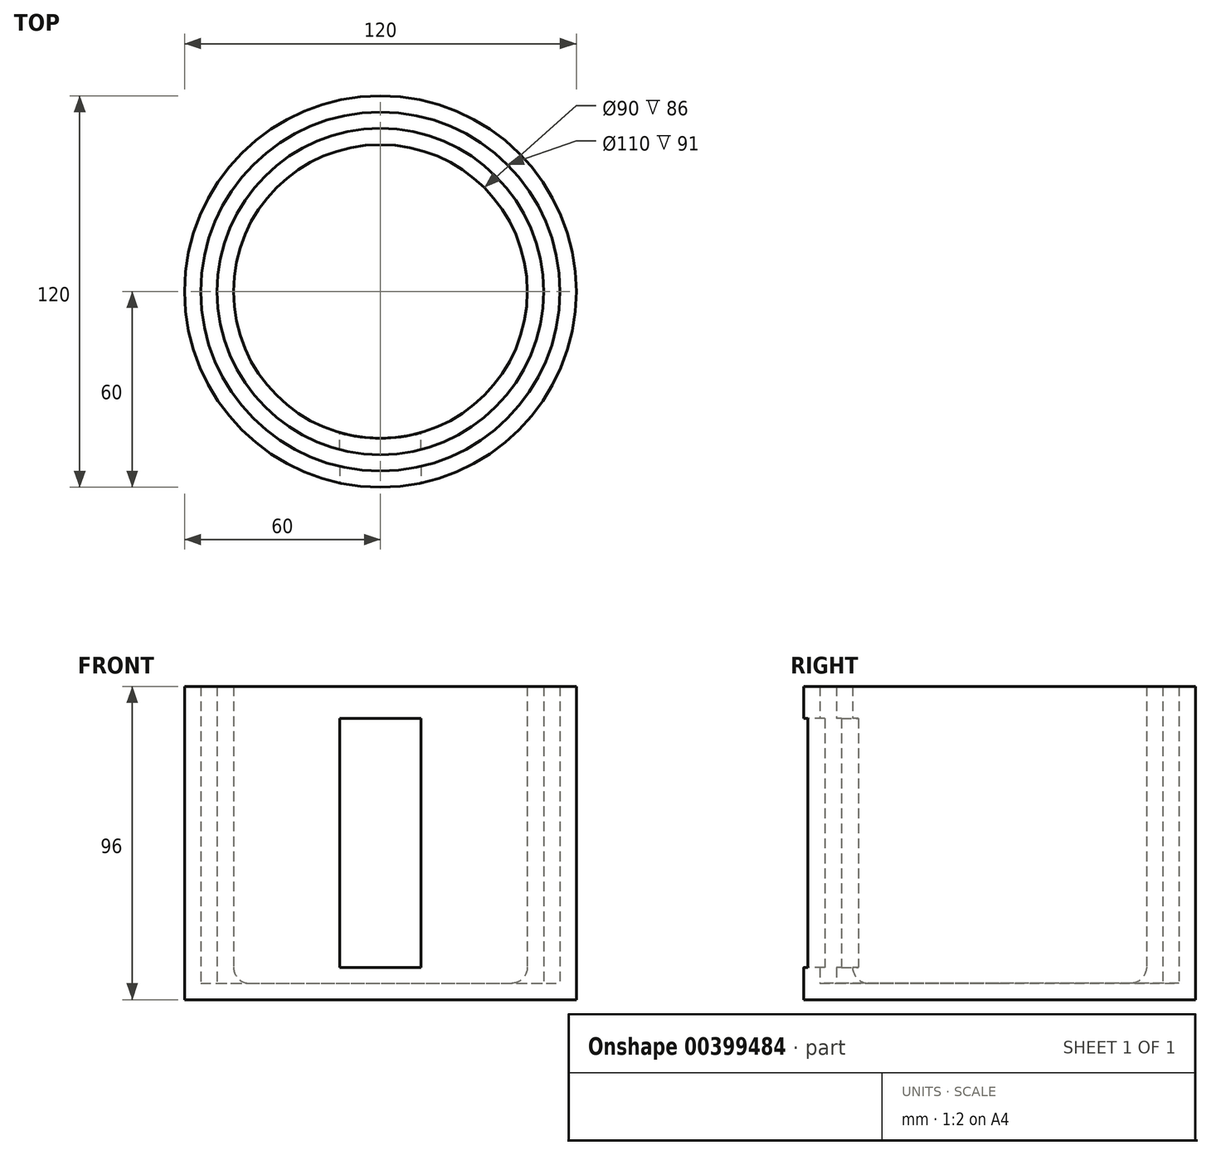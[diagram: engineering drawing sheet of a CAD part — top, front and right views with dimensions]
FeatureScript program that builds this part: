
annotation { "Feature Type Name" : "Feature", "Feature Type Description" : "" }
export const myFeature = defineFeature(function(context is Context, id is Id, definition is map)
    precondition{}
    {
        {
            var Q0;
            Q0=qCreatedBy(makeId("Front.planeOp"),FACE);
            var sketch = newSketch(context, id + "F0", { "sketchPlane" : qUnion([Q0])});
            skLineSegment(sketch, "E0", {"start": v(0, 0) * mm, "end": v(60, 0) * mm});
            skLineSegment(sketch, "E1", {"start": v(60, 0) * mm, "end": v(60, 96) * mm});
            skLineSegment(sketch, "E2.0", {"start": v(55, 5) * mm, "end": v(55, 96) * mm});
            skLineSegment(sketch, "E2.1", {"start": v(0, 5) * mm, "end": v(40, 5) * mm});
            skLineSegment(sketch, "E3", {"start": v(60, 96) * mm, "end": v(55, 96) * mm});
            skLineSegment(sketch, "E4", {"start": v(0, 0) * mm, "end": v(0, 5) * mm});
            skLineSegment(sketch, "E5.top", {"start": v(45, 96) * mm, "end": v(50, 96) * mm});
            skLineSegment(sketch, "E5.left", {"start": v(45, 10) * mm, "end": v(45, 96) * mm});
            skLineSegment(sketch, "E5.right", {"start": v(50, 5) * mm, "end": v(50, 96) * mm});
            skLineSegment(sketch, "E6.trimOffspring", {"start": v(50, 5) * mm, "end": v(55, 5) * mm});
            skPoint(sketch, "E7.visualSharp", {"position": v(45, 5) * mm});
            skArc(sketch, "E7.filletArc", {"start": v(40, 5) * mm, "mid": v(43.54, 6.46) * mm, "end": v(45, 10) * mm});
            skSolve(sketch);
        }
        {
            var Q0;
            Q0=makeQuery(id+"F0.imprint","IMPRINT",FACE,{"disambiguationData":[TD([[makeQuery(id+"F0.imprint","IMPRINT",EDGE,{"derivedFrom":sQuery(id+"F0.wireOp",EDGE,"E0")}),1.0]])]});
            var Q1;
            Q1=sQuery(id+"F0.wireOp",EDGE,"E4");
            revolve(context, id + "F1", {"entities" : qUnion([Q0]), "axis" : qUnion([Q1]), "revolveType" : RevolveType.FULL});
        }
        {
            var Q0;
            Q0=qCreatedBy(makeId("Front.planeOp"),FACE);
            var sketch = newSketch(context, id + "F2", { "sketchPlane" : qUnion([Q0])});
            skLineSegment(sketch, "E8.0", {"start": v(55, 5) * mm, "end": v(-55, 5) * mm, "construction": true});
            skLineSegment(sketch, "E9", {"start": v(-60, 0) * mm, "end": v(-60, 96) * mm, "construction": true});
            skLineSegment(sketch, "E10.bottom", {"start": v(12.5, 86.17) * mm, "end": v(-12.5, 86.17) * mm});
            skLineSegment(sketch, "E10.top", {"start": v(12.5, 9.83) * mm, "end": v(-12.5, 9.83) * mm});
            skLineSegment(sketch, "E10.left", {"start": v(12.5, 86.17) * mm, "end": v(12.5, 9.83) * mm});
            skLineSegment(sketch, "E10.right", {"start": v(-12.5, 86.17) * mm, "end": v(-12.5, 9.83) * mm});
            skPoint(sketch, "E10.middle", {"position": v(0, 48) * mm});
            skPoint(sketch, "E10.middle.positionSnap0", {"position": v(-60, 48) * mm});
            skPoint(sketch, "E10.centerSnap0", {"position": v(-60, 48) * mm});
            skSolve(sketch);
        }
        {
            var Q0;
            Q0=qSketchRegion(id+"F2",true);
            var Q1;
            Q1=makeQuery(id+"F1.opRevolve","SWEPT_FACE",FACE,{"disambiguationData":[OSD([sQuery(id+"F0.wireOp",EDGE,"E5.right")])]});
            extrude(context, id + "F3", {"entities" : qUnion([Q0]), "operationType" : NewBodyOperationType.REMOVE, "endBound" : BoundingType.UP_TO_SURFACE, "endBoundEntityFace" : qUnion([Q1]), "depth" : 25 * mm});
        }
        {
            var Q0;
            Q0=qCreatedBy(makeId("Front.planeOp"),FACE);
            cPlane(context, id + "F4", {"entities" : qUnion([Q0]), "cplaneType" : CPlaneType.OFFSET, "offset" : 75 * mm, "width" : 150 * mm, "height" : 150 * mm});
        }
        {
            var Q0;
            Q0=qCreatedBy(id+"F4.planeOp",FACE);
            var sketch = newSketch(context, id + "F5", { "sketchPlane" : qUnion([Q0])});
            skLineSegment(sketch, "E11.0", {"start": v(-12.5, 86.17) * mm, "end": v(-12.5, 9.83) * mm});
            skPoint(sketch, "E12.0", {"position": v(0, 86.17) * mm});
            skLineSegment(sketch, "E13.0", {"start": v(12.5, 86.17) * mm, "end": v(-12.5, 86.17) * mm});
            skLineSegment(sketch, "E14.0", {"start": v(12.5, 86.17) * mm, "end": v(12.5, 9.83) * mm});
            skLineSegment(sketch, "E15.0", {"start": v(12.5, 9.83) * mm, "end": v(-12.5, 9.83) * mm});
            skSolve(sketch);
        }
        {
            var Q0;
            Q0=qSketchRegion(id+"F5",true);
            var Q1;
            Q1=makeQuery(id+"F1.opRevolve","SWEPT_FACE",FACE,{"disambiguationData":[OSD([sQuery(id+"F0.wireOp",EDGE,"E2.0")])]});
            extrude(context, id + "F6", {"entities" : qUnion([Q0]), "operationType" : NewBodyOperationType.REMOVE, "endBound" : BoundingType.UP_TO_SURFACE, "oppositeDirection" : true, "endBoundEntityFace" : qUnion([Q1]), "depth" : 25 * mm});
        }
    });
